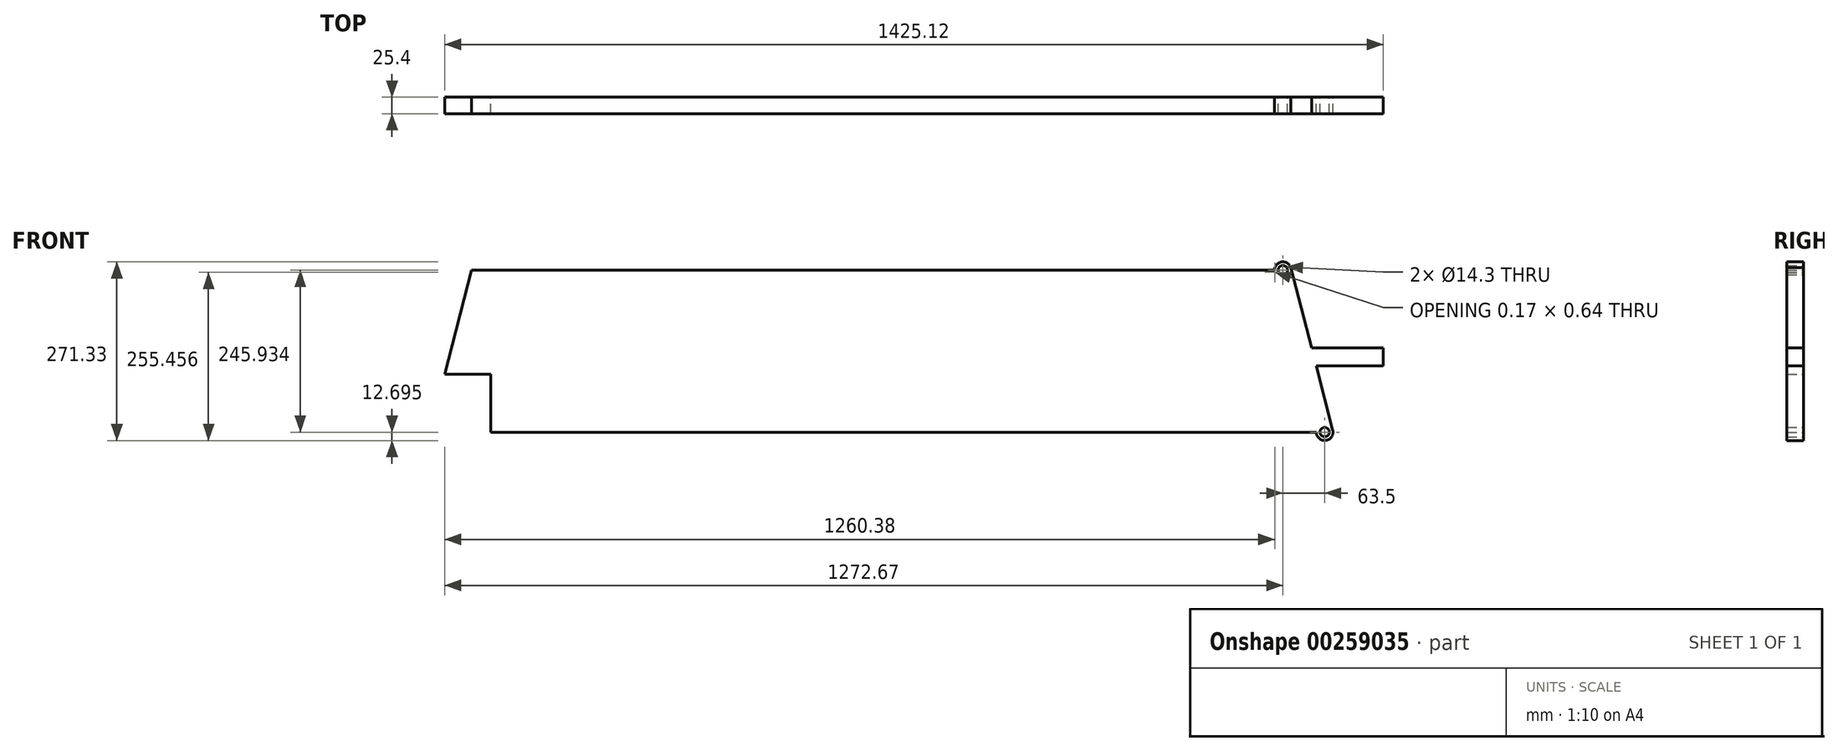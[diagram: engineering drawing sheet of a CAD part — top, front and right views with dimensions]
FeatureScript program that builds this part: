
annotation { "Feature Type Name" : "Feature", "Feature Type Description" : "" }
export const myFeature = defineFeature(function(context is Context, id is Id, definition is map)
    precondition{}
    {
        {
            var Q0;
            Q0=qCreatedBy(makeId("Front.planeOp"),FACE);
            var sketch = newSketch(context, id + "F0", { "sketchPlane" : qUnion([Q0])});
            skCircle(sketch, "E0", {"center": v(-31.75, 29.12) * mm, "radius": 7.15 * mm});
            skCircle(sketch, "E1", {"center": v(31.75, -216.81) * mm, "radius": 7.15 * mm});
            skCircle(sketch, "E2", {"center": v(-31.75, 29.12) * mm, "radius": 12.7 * mm});
            skCircle(sketch, "E3", {"center": v(31.75, -216.81) * mm, "radius": 12.7 * mm});
            skLineSegment(sketch, "E4", {"start": v(-44.13, 26.27) * mm, "end": v(19.45, -219.99) * mm});
            skLineSegment(sketch, "E5", {"start": v(-19.73, 33.23) * mm, "end": v(44.05, -213.64) * mm});
            skLineSegment(sketch, "E6", {"start": v(120.7, -88.95) * mm, "end": v(120.7, -115.95) * mm});
            skLineSegment(sketch, "E7", {"start": v(120.7, -88.95) * mm, "end": v(11.83, -88.95) * mm});
            skLineSegment(sketch, "E8", {"start": v(120.7, -115.95) * mm, "end": v(18.8, -115.95) * mm});
            skLineSegment(sketch, "E9", {"start": v(-31.75, 29.12) * mm, "end": v(91.72, -449.1) * mm});
            skLineSegment(sketch, "E10", {"start": v(82.6, -540.7) * mm, "end": v(82.77, -540.7) * mm});
            skLineSegment(sketch, "E11", {"start": v(-31.75, 29.12) * mm, "end": v(-1263.65, 29.12) * mm});
            skLineSegment(sketch, "E12", {"start": v(-1263.65, 29.12) * mm, "end": v(-1327.15, -216.81) * mm});
            skLineSegment(sketch, "E13", {"start": v(-6, -128.76) * mm, "end": v(-1304.42, -128.76) * mm});
            skLineSegment(sketch, "E14", {"start": v(-1304.42, -128.76) * mm, "end": v(-1431.42, -128.76) * mm});
            skLineSegment(sketch, "E15", {"start": v(-1234.54, -568.03) * mm, "end": v(-1234.54, -128.76) * mm});
            skLineSegment(sketch, "E16", {"start": v(-1431.42, -128.76) * mm, "end": v(-1507.62, -128.76) * mm});
            skLineSegment(sketch, "E17", {"start": v(-1507.62, -128.76) * mm, "end": v(-1304.42, -128.76) * mm});
            skLineSegment(sketch, "E18", {"start": v(-1406.02, -128.76) * mm, "end": v(-1406.02, -572.6) * mm});
            skLineSegment(sketch, "E19", {"start": v(-1406.02, -128.76) * mm, "end": v(-1558.54, -128.76) * mm});
            skPoint(sketch, "E20.endSnap0", {"position": v(120.7, -102.45) * mm});
            skLineSegment(sketch, "E21", {"start": v(9.49, -79.88) * mm, "end": v(263.62, -79.88) * mm});
            skLineSegment(sketch, "E22", {"start": v(-1263.65, 29.12) * mm, "end": v(-1419.01, -572.6) * mm});
            skLineSegment(sketch, "E23", {"start": v(-1419.01, -572.6) * mm, "end": v(-1406.02, -572.6) * mm});
            skLineSegment(sketch, "E24", {"start": v(-647.7, 29.12) * mm, "end": v(-850.9, 29.12) * mm});
            skLineSegment(sketch, "E25", {"start": v(-1327.15, -216.81) * mm, "end": v(31.75, -216.81) * mm});
            skLineSegment(sketch, "E26", {"start": v(-647.7, -216.81) * mm, "end": v(-723.9, -216.81) * mm});
            skSolve(sketch);
        }
        {
            var Q0;
            {var subQ1=sQuery(id+"F0.wireOp",EDGE,"E7");Q0=makeQuery(id+"F0.imprint","IMPRINT",FACE,{"disambiguationData":[TD([[makeQuery(id+"F0.imprint","IMPRINT",EDGE,{"derivedFrom":subQ1}),1.0]])]});}
            var Q1;
            {var subQ0=sQuery(id+"F0.wireOp",EDGE,"E8");var subQ1=sQuery(id+"F0.wireOp",EDGE,"E5");var subQ2=makeQuery(id+"F0.imprint","INTERSECT",VERTEX,{"derivedFrom":[subQ1,subQ0]});Q1=makeQuery(id+"F0.imprint","IMPRINT",FACE,{"disambiguationData":[TD([[makeQuery(id+"F0.imprint","IMPRINT",EDGE,{"disambiguationData":[TD([[subQ2,1.0]])],"derivedFrom":subQ1}),1.0]])]});}
            var Q2;
            {var subQ3=sQuery(id+"F0.wireOp",EDGE,"E3");var subQ5=sQuery(id+"F0.wireOp",EDGE,"E5");var subQ8=makeQuery(id+"F0.imprint","INTERSECT",VERTEX,{"derivedFrom":[subQ3,subQ5]});Q2=makeQuery(id+"F0.imprint","IMPRINT",FACE,{"disambiguationData":[TD([[makeQuery(id+"F0.imprint","IMPRINT",EDGE,{"disambiguationData":[TD([[subQ8,-1.0]])],"derivedFrom":subQ3}),-1.0]])]});}
            var Q3;
            {var subQ1=sQuery(id+"F0.wireOp",EDGE,"E9");var subQ5=sQuery(id+"F0.wireOp",EDGE,"E3");var subQ6=makeQuery(id+"F0.imprint","INTERSECT",VERTEX,{"disambiguationData":[OD(1.0)],"derivedFrom":[subQ5,subQ1]});Q3=makeQuery(id+"F0.imprint","IMPRINT",FACE,{"disambiguationData":[TD([[makeQuery(id+"F0.imprint","IMPRINT",EDGE,{"disambiguationData":[TD([[subQ6,-1.0]])],"derivedFrom":subQ5}),-1.0]])]});}
            var Q4;
            {var subQ0=sQuery(id+"F0.wireOp",EDGE,"E4");var subQ1=sQuery(id+"F0.wireOp",EDGE,"E2");var subQ2=makeQuery(id+"F0.imprint","INTERSECT",VERTEX,{"disambiguationData":[OD(1.0)],"derivedFrom":[subQ1,subQ0]});Q4=makeQuery(id+"F0.imprint","IMPRINT",FACE,{"disambiguationData":[TD([[makeQuery(id+"F0.imprint","IMPRINT",EDGE,{"disambiguationData":[TD([[subQ2,-1.0]])],"derivedFrom":subQ1}),-1.0]])]});}
            var Q5;
            {var subQ3=sQuery(id+"F0.wireOp",EDGE,"E2");var subQ5=sQuery(id+"F0.wireOp",EDGE,"E5");var subQ8=makeQuery(id+"F0.imprint","INTERSECT",VERTEX,{"disambiguationData":[OD(1.0)],"derivedFrom":[subQ3,subQ5]});Q5=makeQuery(id+"F0.imprint","IMPRINT",FACE,{"disambiguationData":[TD([[makeQuery(id+"F0.imprint","IMPRINT",EDGE,{"disambiguationData":[TD([[subQ8,1.0]])],"derivedFrom":subQ3}),-1.0]])]});}
            var Q6;
            {var subQ4=sQuery(id+"F0.wireOp",EDGE,"E9");var subQ6=sQuery(id+"F0.wireOp",EDGE,"E0");var subQ7=makeQuery(id+"F0.imprint","INTERSECT",VERTEX,{"derivedFrom":[subQ6,subQ4]});Q6=makeQuery(id+"F0.imprint","IMPRINT",FACE,{"disambiguationData":[TD([[makeQuery(id+"F0.imprint","IMPRINT",EDGE,{"disambiguationData":[TD([[subQ7,-1.0]])],"derivedFrom":subQ6}),-1.0]])]});}
            var Q7;
            {var subQ0=sQuery(id+"F0.wireOp",EDGE,"E9");var subQ1=sQuery(id+"F0.wireOp",EDGE,"E1");var subQ2=makeQuery(id+"F0.imprint","INTERSECT",VERTEX,{"disambiguationData":[OD(0.0)],"derivedFrom":[subQ1,subQ0]});Q7=makeQuery(id+"F0.imprint","IMPRINT",FACE,{"disambiguationData":[TD([[makeQuery(id+"F0.imprint","IMPRINT",EDGE,{"disambiguationData":[TD([[subQ2,1.0]])],"derivedFrom":subQ1}),-1.0]])]});}
            var Q8;
            {var subQ4=sQuery(id+"F0.wireOp",EDGE,"iI34NFCZ-dKQS-DYyj-2k0U-teQh5JN0447x");var subQ5=sQuery(id+"F0.wireOp",EDGE,"E1");var subQ6=makeQuery(id+"F0.imprint","INTERSECT",VERTEX,{"derivedFrom":[subQ5,subQ4]});Q8=makeQuery(id+"F0.imprint","IMPRINT",FACE,{"disambiguationData":[TD([[makeQuery(id+"F0.imprint","IMPRINT",EDGE,{"disambiguationData":[TD([[subQ6,-1.0]])],"derivedFrom":subQ5}),-1.0]])]});}
            var Q9;
            {var subQ0=sQuery(id+"F0.wireOp",EDGE,"iI34NFCZ-dKQS-DYyj-2k0U-teQh5JN0447x");var subQ1=sQuery(id+"F0.wireOp",EDGE,"E1");var subQ2=makeQuery(id+"F0.imprint","INTERSECT",VERTEX,{"derivedFrom":[subQ1,subQ0]});Q9=makeQuery(id+"F0.imprint","IMPRINT",FACE,{"disambiguationData":[TD([[makeQuery(id+"F0.imprint","IMPRINT",EDGE,{"disambiguationData":[TD([[subQ2,1.0]])],"derivedFrom":subQ1}),-1.0]])]});}
            var Q10;
            {var subQ0=sQuery(id+"F0.wireOp",EDGE,"101x5Hxq-zcrE-CQXI-RwYv-nPtihcfaPfau");var subQ1=sQuery(id+"F0.wireOp",EDGE,"E8");var subQ2=makeQuery(id+"F0.imprint","INTERSECT",VERTEX,{"derivedFrom":[subQ1,subQ0]});Q10=makeQuery(id+"F0.imprint","IMPRINT",FACE,{"disambiguationData":[TD([[makeQuery(id+"F0.imprint","IMPRINT",EDGE,{"disambiguationData":[TD([[subQ2,-1.0]])],"derivedFrom":subQ1}),-1.0]])]});}
            var Q11;
            {var subQ4=sQuery(id+"F0.wireOp",EDGE,"E9");var subQ8=sQuery(id+"F0.wireOp",EDGE,"E0");var subQ9=makeQuery(id+"F0.imprint","INTERSECT",VERTEX,{"derivedFrom":[subQ8,subQ4]});Q11=makeQuery(id+"F0.imprint","IMPRINT",FACE,{"disambiguationData":[TD([[makeQuery(id+"F0.imprint","IMPRINT",EDGE,{"disambiguationData":[TD([[subQ9,1.0]])],"derivedFrom":subQ8}),-1.0]])]});}
            var Q12;
            {var subQ3=sQuery(id+"F0.wireOp",EDGE,"E1");var subQ6=sQuery(id+"F0.wireOp",EDGE,"E25");var subQ8=makeQuery(id+"F0.imprint","INTERSECT",VERTEX,{"derivedFrom":[subQ3,subQ6]});Q12=makeQuery(id+"F0.imprint","IMPRINT",FACE,{"disambiguationData":[TD([[makeQuery(id+"F0.imprint","IMPRINT",EDGE,{"disambiguationData":[TD([[subQ8,-1.0]])],"derivedFrom":subQ3}),-1.0]])]});}
            extrude(context, id + "F1", {"entities" : qUnion([Q0, Q1, Q2, Q3, Q4, Q5, Q6, Q7, Q8, Q9, Q10, Q11, Q12]), "depth" : 25.4 * mm});
        }
    });
